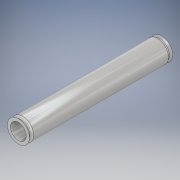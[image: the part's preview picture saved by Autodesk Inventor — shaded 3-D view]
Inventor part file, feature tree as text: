
AUTODESK INVENTOR PART (.ipt)
format: ipt  version: 2019 (Build 230136000, 136)  size: 138,752 bytes
history: native  units: mm
features: revolve x1, sketch x1
ambient origin geometry x8: Origin, YZ Plane, XZ Plane, XY Plane, X Axis, Y Axis, Z Axis, Center Point
bodies: Solid1 (feature_tree)
feature tree (2):
  revolve  "Revolution1"  [1 undecoded]
  sketch  "Sketch1"  dims[d7=90.0deg d15=3.0mm d16=7.5mm]
note: 1 required parameter value undecoded (feature->parameter linkage not recoverable at this tier; creation-order binding heuristic only, values carry confidence <= 0.55)
